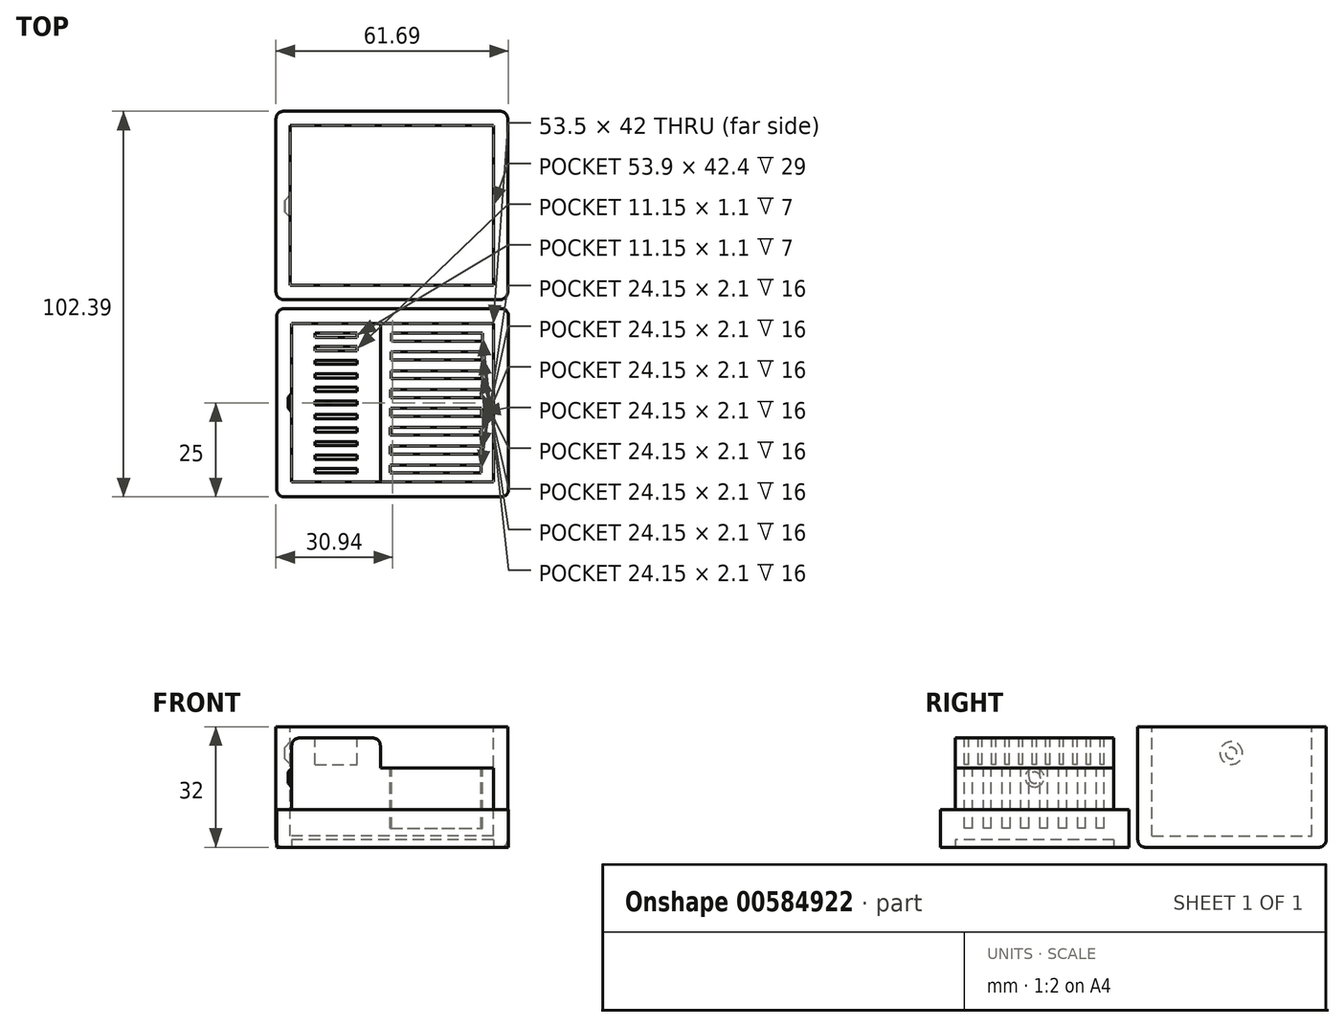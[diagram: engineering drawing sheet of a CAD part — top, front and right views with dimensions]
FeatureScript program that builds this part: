
annotation { "Feature Type Name" : "Feature", "Feature Type Description" : "" }
export const myFeature = defineFeature(function(context is Context, id is Id, definition is map)
    precondition{}
    {
        {
            var Q0;
            Q0=qCreatedBy(makeId("Top.planeOp"),FACE);
            var sketch = newSketch(context, id + "F0", { "sketchPlane" : qUnion([Q0])});
            skLineSegment(sketch, "E0.bottom", {"start": v(30.75, -25) * mm, "end": v(-30.75, -25) * mm});
            skLineSegment(sketch, "E0.top", {"start": v(30.75, 25) * mm, "end": v(-30.75, 25) * mm});
            skLineSegment(sketch, "E0.left", {"start": v(30.75, -25) * mm, "end": v(30.75, 25) * mm});
            skLineSegment(sketch, "E0.right", {"start": v(-30.75, -25) * mm, "end": v(-30.75, 25) * mm});
            skPoint(sketch, "E0.middle", {"position": v(0, 0) * mm});
            skSolve(sketch);
        }
        {
            var Q0;
            Q0 = qSketchRegion(id + "F0", true);
            extrude(context, id + "F1", {"entities" : qUnion([Q0]), "depth" : 21 * mm, "offsetDistance" : 25 * mm});
        }
        {
            var Q0;
            Q0=makeQuery(id+"F1.opExtrude","CAP_FACE",FACE,{"disambiguationData":[OSD([sQuery(id+"F0.wireOp",EDGE,"E0.bottom"),sQuery(id+"F0.wireOp",EDGE,"E0.top"),sQuery(id+"F0.wireOp",EDGE,"E0.left"),sQuery(id+"F0.wireOp",EDGE,"E0.right")])],"isStart":false});
            var sketch = newSketch(context, id + "F2", { "sketchPlane" : qUnion([Q0])});
            skLineSegment(sketch, "E1.bottom", {"start": v(26.75, -21) * mm, "end": v(-26.75, -21) * mm});
            skLineSegment(sketch, "E1.top", {"start": v(26.75, 21) * mm, "end": v(-26.75, 21) * mm});
            skLineSegment(sketch, "E1.left", {"start": v(26.75, -21) * mm, "end": v(26.75, 21) * mm});
            skLineSegment(sketch, "E1.right", {"start": v(-26.75, -21) * mm, "end": v(-26.75, 21) * mm});
            skPoint(sketch, "E1.middle", {"position": v(0, 0) * mm});
            skSolve(sketch);
        }
        {
            var Q0;
            Q0=makeQuery(id+"F2.imprint","IMPRINT",FACE,{"disambiguationData":[TD([[makeQuery(id+"F2.imprint","IMPRINT",EDGE,{"derivedFrom":sQuery(id+"F2.wireOp",EDGE,"E1.bottom")}),1.0]])]});
            extrude(context, id + "F3", {"entities" : qUnion([Q0]), "operationType" : NewBodyOperationType.REMOVE, "oppositeDirection" : true, "depth" : 11 * mm, "offsetDistance" : 25 * mm});
        }
        {
            var Q0;
            Q0=makeQuery(id+"F1.opExtrude","CAP_FACE",FACE,{"disambiguationData":[OSD([sQuery(id+"F0.wireOp",EDGE,"E0.bottom"),sQuery(id+"F0.wireOp",EDGE,"E0.top"),sQuery(id+"F0.wireOp",EDGE,"E0.left"),sQuery(id+"F0.wireOp",EDGE,"E0.right")])],"isStart":false});
            var sketch = newSketch(context, id + "F4", { "sketchPlane" : qUnion([Q0])});
            skLineSegment(sketch, "E2.bottom", {"start": v(0, 21) * mm, "end": v(-26.75, 21) * mm});
            skLineSegment(sketch, "E2.top", {"start": v(0, -21) * mm, "end": v(-26.75, -21) * mm});
            skLineSegment(sketch, "E2.right", {"start": v(-26.75, 21) * mm, "end": v(-26.75, -21) * mm});
            skLineSegment(sketch, "E3.bottom", {"start": v(-26.75, 21) * mm, "end": v(-3.25, 21) * mm});
            skLineSegment(sketch, "E3.top", {"start": v(-26.75, -21) * mm, "end": v(-3.25, -21) * mm});
            skLineSegment(sketch, "E3.right", {"start": v(-3.25, 21) * mm, "end": v(-3.25, -21) * mm});
            skSolve(sketch);
        }
        {
            var Q0;
            Q0 = qSketchRegion(id + "F4", true);
            extrude(context, id + "F5", {"entities" : qUnion([Q0]), "operationType" : NewBodyOperationType.ADD, "depth" : 8 * mm, "offsetDistance" : 25 * mm});
        }
        {
            var Q0;
            Q0=makeQuery(id+"F5.opExtrude","CAP_FACE",FACE,{"disambiguationData":[OSD([sQuery(id+"F4.wireOp",EDGE,"E3.bottom"),sQuery(id+"F4.wireOp",EDGE,"E3.top"),sQuery(id+"F4.wireOp",EDGE,"E2.right"),sQuery(id+"F4.wireOp",EDGE,"E3.right")])],"isStart":false});
            var sketch = newSketch(context, id + "F6", { "sketchPlane" : qUnion([Q0]), "disableImprinting" : false});
            skLineSegment(sketch, "E4.bottom", {"start": v(-20.57, 18.5) * mm, "end": v(-9.42, 18.5) * mm});
            skLineSegment(sketch, "E4.top", {"start": v(-20.57, 17.4) * mm, "end": v(-9.42, 17.4) * mm});
            skLineSegment(sketch, "E4.left", {"start": v(-20.57, 18.5) * mm, "end": v(-20.57, 17.4) * mm});
            skLineSegment(sketch, "E4.right", {"start": v(-9.42, 18.5) * mm, "end": v(-9.42, 17.4) * mm});
            skLineSegment(sketch, "E5.1.0.0", {"start": v(-20.57, 14.9) * mm, "end": v(-9.42, 14.9) * mm});
            skLineSegment(sketch, "E5.1.0.1", {"start": v(-20.57, 13.8) * mm, "end": v(-9.42, 13.8) * mm});
            skLineSegment(sketch, "E5.1.0.2", {"start": v(-9.42, 14.9) * mm, "end": v(-9.42, 13.8) * mm});
            skLineSegment(sketch, "E5.1.0.3", {"start": v(-20.57, 14.9) * mm, "end": v(-20.57, 13.8) * mm});
            skLineSegment(sketch, "E5.2.0.0", {"start": v(-20.57, 11.3) * mm, "end": v(-9.42, 11.3) * mm});
            skLineSegment(sketch, "E5.2.0.1", {"start": v(-20.57, 10.2) * mm, "end": v(-9.42, 10.2) * mm});
            skLineSegment(sketch, "E5.2.0.2", {"start": v(-9.42, 11.3) * mm, "end": v(-9.42, 10.2) * mm});
            skLineSegment(sketch, "E5.2.0.3", {"start": v(-20.57, 11.3) * mm, "end": v(-20.57, 10.2) * mm});
            skLineSegment(sketch, "E5.3.0.0", {"start": v(-20.57, 7.7) * mm, "end": v(-9.42, 7.7) * mm});
            skLineSegment(sketch, "E5.3.0.1", {"start": v(-20.57, 6.6) * mm, "end": v(-9.42, 6.6) * mm});
            skLineSegment(sketch, "E5.3.0.2", {"start": v(-9.42, 7.7) * mm, "end": v(-9.42, 6.6) * mm});
            skLineSegment(sketch, "E5.3.0.3", {"start": v(-20.57, 7.7) * mm, "end": v(-20.57, 6.6) * mm});
            skLineSegment(sketch, "E5.4.0.0", {"start": v(-20.57, 4.1) * mm, "end": v(-9.42, 4.1) * mm});
            skLineSegment(sketch, "E5.4.0.1", {"start": v(-20.57, 3) * mm, "end": v(-9.42, 3) * mm});
            skLineSegment(sketch, "E5.4.0.2", {"start": v(-9.42, 4.1) * mm, "end": v(-9.42, 3) * mm});
            skLineSegment(sketch, "E5.4.0.3", {"start": v(-20.57, 4.1) * mm, "end": v(-20.57, 3) * mm});
            skLineSegment(sketch, "E5.5.0.0", {"start": v(-20.57, 0.5) * mm, "end": v(-9.42, 0.5) * mm});
            skLineSegment(sketch, "E5.5.0.1", {"start": v(-20.57, -0.6) * mm, "end": v(-9.42, -0.6) * mm});
            skLineSegment(sketch, "E5.5.0.2", {"start": v(-9.42, 0.5) * mm, "end": v(-9.42, -0.6) * mm});
            skLineSegment(sketch, "E5.5.0.3", {"start": v(-20.57, 0.5) * mm, "end": v(-20.57, -0.6) * mm});
            skLineSegment(sketch, "E5.6.0.0", {"start": v(-20.57, -3.1) * mm, "end": v(-9.42, -3.1) * mm});
            skLineSegment(sketch, "E5.6.0.1", {"start": v(-20.57, -4.2) * mm, "end": v(-9.42, -4.2) * mm});
            skLineSegment(sketch, "E5.6.0.2", {"start": v(-9.42, -3.1) * mm, "end": v(-9.42, -4.2) * mm});
            skLineSegment(sketch, "E5.6.0.3", {"start": v(-20.57, -3.1) * mm, "end": v(-20.57, -4.2) * mm});
            skLineSegment(sketch, "E5.7.0.0", {"start": v(-20.57, -6.7) * mm, "end": v(-9.42, -6.7) * mm});
            skLineSegment(sketch, "E5.7.0.1", {"start": v(-20.57, -7.8) * mm, "end": v(-9.42, -7.8) * mm});
            skLineSegment(sketch, "E5.7.0.2", {"start": v(-9.42, -6.7) * mm, "end": v(-9.42, -7.8) * mm});
            skLineSegment(sketch, "E5.7.0.3", {"start": v(-20.57, -6.7) * mm, "end": v(-20.57, -7.8) * mm});
            skLineSegment(sketch, "E5.8.0.0", {"start": v(-20.57, -10.3) * mm, "end": v(-9.42, -10.3) * mm});
            skLineSegment(sketch, "E5.8.0.1", {"start": v(-20.57, -11.4) * mm, "end": v(-9.42, -11.4) * mm});
            skLineSegment(sketch, "E5.8.0.2", {"start": v(-9.42, -10.3) * mm, "end": v(-9.42, -11.4) * mm});
            skLineSegment(sketch, "E5.8.0.3", {"start": v(-20.57, -10.3) * mm, "end": v(-20.57, -11.4) * mm});
            skLineSegment(sketch, "E5.9.0.0", {"start": v(-20.57, -13.9) * mm, "end": v(-9.42, -13.9) * mm});
            skLineSegment(sketch, "E5.9.0.1", {"start": v(-20.57, -15) * mm, "end": v(-9.42, -15) * mm});
            skLineSegment(sketch, "E5.9.0.2", {"start": v(-9.42, -13.9) * mm, "end": v(-9.42, -15) * mm});
            skLineSegment(sketch, "E5.9.0.3", {"start": v(-20.57, -13.9) * mm, "end": v(-20.57, -15) * mm});
            skLineSegment(sketch, "E5.10.0.0", {"start": v(-20.57, -17.5) * mm, "end": v(-9.42, -17.5) * mm});
            skLineSegment(sketch, "E5.10.0.1", {"start": v(-20.57, -18.6) * mm, "end": v(-9.42, -18.6) * mm});
            skLineSegment(sketch, "E5.10.0.2", {"start": v(-9.42, -17.5) * mm, "end": v(-9.42, -18.6) * mm});
            skLineSegment(sketch, "E5.10.0.3", {"start": v(-20.57, -17.5) * mm, "end": v(-20.57, -18.6) * mm});
            skLineSegment(sketch, "E5.direction1", {"start": v(-17.32, 17.5) * mm, "end": v(-17.32, 13.9) * mm, "construction": true});
            skSolve(sketch);
        }
        {
            var Q0;
            Q0 = qSketchRegion(id + "F6", true);
            extrude(context, id + "F7", {"entities" : qUnion([Q0]), "operationType" : NewBodyOperationType.REMOVE, "oppositeDirection" : true, "depth" : 7 * mm, "offsetDistance" : 25 * mm});
        }
        {
            var Q0;
            Q0=makeQuery(id+"F1.opExtrude","CAP_FACE",FACE,{"disambiguationData":[OSD([sQuery(id+"F0.wireOp",EDGE,"E0.bottom"),sQuery(id+"F0.wireOp",EDGE,"E0.top"),sQuery(id+"F0.wireOp",EDGE,"E0.left"),sQuery(id+"F0.wireOp",EDGE,"E0.right")])],"isStart":false});
            var sketch = newSketch(context, id + "F8", { "sketchPlane" : qUnion([Q0])});
            skLineSegment(sketch, "E6.bottom", {"start": v(-0.33, 18.5) * mm, "end": v(23.82, 18.5) * mm});
            skLineSegment(sketch, "E6.top", {"start": v(-0.33, 16.4) * mm, "end": v(23.82, 16.4) * mm});
            skLineSegment(sketch, "E6.left", {"start": v(-0.33, 18.5) * mm, "end": v(-0.33, 16.4) * mm});
            skLineSegment(sketch, "E6.right", {"start": v(23.82, 18.5) * mm, "end": v(23.82, 16.4) * mm});
            skLineSegment(sketch, "E7.1.0.0", {"start": v(-0.38, 11.4) * mm, "end": v(23.77, 11.4) * mm});
            skLineSegment(sketch, "E7.1.0.1", {"start": v(23.77, 13.5) * mm, "end": v(23.77, 11.4) * mm});
            skLineSegment(sketch, "E7.1.0.2", {"start": v(-0.38, 13.5) * mm, "end": v(-0.38, 11.4) * mm});
            skLineSegment(sketch, "E7.1.0.3", {"start": v(-0.38, 13.5) * mm, "end": v(23.77, 13.5) * mm});
            skLineSegment(sketch, "E7.2.0.0", {"start": v(-0.44, 6.4) * mm, "end": v(23.71, 6.4) * mm});
            skLineSegment(sketch, "E7.2.0.1", {"start": v(23.71, 8.5) * mm, "end": v(23.71, 6.4) * mm});
            skLineSegment(sketch, "E7.2.0.2", {"start": v(-0.44, 8.5) * mm, "end": v(-0.44, 6.4) * mm});
            skLineSegment(sketch, "E7.2.0.3", {"start": v(-0.44, 8.5) * mm, "end": v(23.71, 8.5) * mm});
            skLineSegment(sketch, "E7.direction1", {"start": v(-0.33, 16.4) * mm, "end": v(-0.38, 11.4) * mm, "construction": true});
            skLineSegment(sketch, "E8.0.3.0", {"start": v(-0.5, 1.4) * mm, "end": v(23.66, 1.4) * mm});
            skLineSegment(sketch, "E8.3.3.0", {"start": v(23.66, 3.5) * mm, "end": v(23.66, 1.4) * mm});
            skLineSegment(sketch, "E8.6.3.0", {"start": v(-0.5, 3.5) * mm, "end": v(-0.5, 1.4) * mm});
            skLineSegment(sketch, "E8.9.3.0", {"start": v(-0.5, 3.5) * mm, "end": v(23.66, 3.5) * mm});
            skLineSegment(sketch, "E8.0.4.0", {"start": v(-0.55, -3.6) * mm, "end": v(23.6, -3.6) * mm});
            skLineSegment(sketch, "E8.3.4.0", {"start": v(23.6, -1.5) * mm, "end": v(23.6, -3.6) * mm});
            skLineSegment(sketch, "E8.6.4.0", {"start": v(-0.55, -1.5) * mm, "end": v(-0.55, -3.6) * mm});
            skLineSegment(sketch, "E8.9.4.0", {"start": v(-0.55, -1.5) * mm, "end": v(23.6, -1.5) * mm});
            skLineSegment(sketch, "E8.0.5.0", {"start": v(-0.6, -8.6) * mm, "end": v(23.55, -8.6) * mm});
            skLineSegment(sketch, "E8.3.5.0", {"start": v(23.55, -6.5) * mm, "end": v(23.55, -8.6) * mm});
            skLineSegment(sketch, "E8.6.5.0", {"start": v(-0.6, -6.5) * mm, "end": v(-0.6, -8.6) * mm});
            skLineSegment(sketch, "E8.9.5.0", {"start": v(-0.6, -6.5) * mm, "end": v(23.55, -6.5) * mm});
            skLineSegment(sketch, "E9.0.6.0", {"start": v(-0.66, -13.6) * mm, "end": v(23.5, -13.6) * mm});
            skLineSegment(sketch, "E9.3.6.0", {"start": v(23.5, -11.5) * mm, "end": v(23.5, -13.6) * mm});
            skLineSegment(sketch, "E9.6.6.0", {"start": v(-0.66, -11.5) * mm, "end": v(-0.66, -13.6) * mm});
            skLineSegment(sketch, "E9.9.6.0", {"start": v(-0.66, -11.5) * mm, "end": v(23.5, -11.5) * mm});
            skLineSegment(sketch, "E10.0.7.0", {"start": v(-0.71, -18.6) * mm, "end": v(23.44, -18.6) * mm});
            skLineSegment(sketch, "E10.3.7.0", {"start": v(23.44, -16.5) * mm, "end": v(23.44, -18.6) * mm});
            skLineSegment(sketch, "E10.6.7.0", {"start": v(-0.71, -16.5) * mm, "end": v(-0.71, -18.6) * mm});
            skLineSegment(sketch, "E10.9.7.0", {"start": v(-0.71, -16.5) * mm, "end": v(23.44, -16.5) * mm});
            skSolve(sketch);
        }
        {
            var Q0;
            Q0 = qSketchRegion(id + "F8", true);
            extrude(context, id + "F9", {"entities" : qUnion([Q0]), "operationType" : NewBodyOperationType.REMOVE, "oppositeDirection" : true, "depth" : 16 * mm, "offsetDistance" : 25 * mm});
        }
        {
            var Q0;
            Q0=makeQuery(id+"F5.opExtrude","CAP_EDGE",EDGE,{"disambiguationData":[OSD([sQuery(id+"F4.wireOp",EDGE,"E3.right")])],"isStart":false});
            var Q1;
            Q1=makeQuery(id+"F3.boolean.opBoolean","COPY",EDGE,{"derivedFrom":makeQuery(id+"F3.opExtrude","CAP_EDGE",EDGE,{"disambiguationData":[OSD([sQuery(id+"F2.wireOp",EDGE,"E1.left")])],"isStart":true})});
            var Q2;
            Q2=makeQuery(id+"F5.opExtrude","CAP_EDGE",EDGE,{"disambiguationData":[OSD([sQuery(id+"F4.wireOp",EDGE,"E2.right")])],"isStart":false});
            var Q3;
            Q3=makeQuery(id+"F5.opExtrude","CAP_EDGE",EDGE,{"disambiguationData":[OSD([sQuery(id+"F4.wireOp",EDGE,"E3.right")])],"isStart":true});
            var Q4;
            Q4=makeQuery(id+"F1.opExtrude","SWEPT_EDGE",EDGE,{"disambiguationData":[OSD([sQuery(id+"F0.wireOp",EDGE,"E0.bottom"),sQuery(id+"F0.wireOp",EDGE,"E0.right")])]});
            var Q5;
            Q5=makeQuery(id+"F1.opExtrude","SWEPT_EDGE",EDGE,{"disambiguationData":[OSD([sQuery(id+"F0.wireOp",EDGE,"E0.top"),sQuery(id+"F0.wireOp",EDGE,"E0.right")])]});
            var Q6;
            Q6=makeQuery(id+"F1.opExtrude","SWEPT_EDGE",EDGE,{"disambiguationData":[OSD([sQuery(id+"F0.wireOp",EDGE,"E0.bottom"),sQuery(id+"F0.wireOp",EDGE,"E0.left")])]});
            var Q7;
            Q7=makeQuery(id+"F1.opExtrude","SWEPT_EDGE",EDGE,{"disambiguationData":[OSD([sQuery(id+"F0.wireOp",EDGE,"E0.top"),sQuery(id+"F0.wireOp",EDGE,"E0.left")])]});
            var Q8;
            Q8=makeQuery(id+"F5.opExtrude","CAP_EDGE",EDGE,{"disambiguationData":[OSD([sQuery(id+"F4.wireOp",EDGE,"E3.top")])],"isStart":false});
            var Q9;
            Q9=makeQuery(id+"F3.boolean.opBoolean","COPY",EDGE,{"derivedFrom":makeQuery(id+"F3.opExtrude","CAP_EDGE",EDGE,{"disambiguationData":[OSD([sQuery(id+"F2.wireOp",EDGE,"E1.bottom")])],"isStart":true})});
            var Q10;
            Q10=makeQuery(id+"F3.boolean.opBoolean","COPY",EDGE,{"derivedFrom":makeQuery(id+"F3.opExtrude","CAP_EDGE",EDGE,{"disambiguationData":[OSD([sQuery(id+"F2.wireOp",EDGE,"E1.top")])],"isStart":true})});
            var Q11;
            Q11=makeQuery(id+"F5.opExtrude","CAP_EDGE",EDGE,{"disambiguationData":[OSD([sQuery(id+"F4.wireOp",EDGE,"E3.bottom")])],"isStart":false});
            fillet(context, id + "F10", {"entities" : qUnion([Q0, Q1, Q2, Q3, Q4, Q5, Q6, Q7, Q8, Q9, Q10, Q11]), "radius" : 2 * mm, "tangentPropagation" : true, "allowEdgeOverflow" : false});
        }
        {
            var Q0;
            Q0=qCreatedBy(makeId("Top.planeOp"),FACE);
            var sketch = newSketch(context, id + "F11", { "sketchPlane" : qUnion([Q0])});
            skLineSegment(sketch, "E11.bottom", {"start": v(-30.94, 77.39) * mm, "end": v(30.56, 77.39) * mm});
            skLineSegment(sketch, "E11.top", {"start": v(-30.94, 27.39) * mm, "end": v(30.56, 27.39) * mm});
            skLineSegment(sketch, "E11.left", {"start": v(-30.94, 77.39) * mm, "end": v(-30.94, 27.39) * mm});
            skLineSegment(sketch, "E11.right", {"start": v(30.56, 77.39) * mm, "end": v(30.56, 27.39) * mm});
            skSolve(sketch);
        }
        {
            var Q0;
            Q0 = qSketchRegion(id + "F11", true);
            extrude(context, id + "F12", {"entities" : qUnion([Q0]), "depth" : 32 * mm, "offsetDistance" : 25 * mm});
        }
        {
            var Q0;
            Q0=makeQuery(id+"F12.opExtrude","CAP_FACE",FACE,{"disambiguationData":[OSD([sQuery(id+"F11.wireOp",EDGE,"E11.bottom"),sQuery(id+"F11.wireOp",EDGE,"E11.top"),sQuery(id+"F11.wireOp",EDGE,"E11.left"),sQuery(id+"F11.wireOp",EDGE,"E11.right")])],"isStart":false});
            var sketch = newSketch(context, id + "F13", { "sketchPlane" : qUnion([Q0])});
            skLineSegment(sketch, "E12.bottom", {"start": v(26.76, 31.19) * mm, "end": v(-27.14, 31.19) * mm});
            skLineSegment(sketch, "E12.top", {"start": v(26.76, 73.59) * mm, "end": v(-27.14, 73.59) * mm});
            skLineSegment(sketch, "E12.left", {"start": v(26.76, 31.19) * mm, "end": v(26.76, 73.59) * mm});
            skLineSegment(sketch, "E12.right", {"start": v(-27.14, 31.19) * mm, "end": v(-27.14, 73.59) * mm});
            skPoint(sketch, "E12.middle", {"position": v(-0.2, 52.39) * mm});
            skPoint(sketch, "E12.middle.positionSnap0", {"position": v(-30.94, 52.39) * mm});
            skPoint(sketch, "E12.middle.positionSnap1", {"position": v(-0.2, 77.39) * mm});
            skPoint(sketch, "E12.centerSnap0", {"position": v(-30.94, 52.39) * mm});
            skPoint(sketch, "E12.centerSnap1", {"position": v(-0.2, 77.39) * mm});
            skSolve(sketch);
        }
        {
            var Q0;
            Q0 = qSketchRegion(id + "F13", true);
            extrude(context, id + "F14", {"entities" : qUnion([Q0]), "operationType" : NewBodyOperationType.REMOVE, "oppositeDirection" : true, "depth" : 29 * mm, "offsetDistance" : 25 * mm});
        }
        {
            var Q0;
            Q0=makeQuery(id+"F5.boolean.opBoolean","MERGE",FACE,{"derivedFrom":[makeQuery(id+"F3.boolean.opBoolean","COPY",FACE,{"derivedFrom":makeQuery(id+"F3.opExtrude","SWEPT_FACE",FACE,{"disambiguationData":[OSD([sQuery(id+"F2.wireOp",EDGE,"E1.right")])]})}),makeQuery(id+"F5.opExtrude","SWEPT_FACE",FACE,{"disambiguationData":[OSD([sQuery(id+"F4.wireOp",EDGE,"E2.right")])]})]});
            var sketch = newSketch(context, id + "F15", { "sketchPlane" : qUnion([Q0])});
            skCircle(sketch, "E13", {"center": v(0, 18.5) * mm, "radius": 2.5 * mm});
            skPoint(sketch, "E13.centerSnap0", {"position": v(-21, 18.5) * mm});
            skPoint(sketch, "E13.centerSnap1", {"position": v(0, 27) * mm});
            skSolve(sketch);
        }
        {
            var Q0;
            Q0 = qSketchRegion(id + "F15", true);
            extrude(context, id + "F16", {"entities" : qUnion([Q0]), "operationType" : NewBodyOperationType.ADD, "depth" : 1 * mm, "offsetDistance" : 25 * mm, "hasDraft" : true, "draftAngle" : 45 * degree, "draftPullDirection" : true});
        }
        {
            var Q0;
            Q0=makeQuery(id+"F14.boolean.opBoolean","COPY",FACE,{"derivedFrom":makeQuery(id+"F14.opExtrude","SWEPT_FACE",FACE,{"disambiguationData":[OSD([sQuery(id+"F13.wireOp",EDGE,"E12.right")])]})});
            var sketch = newSketch(context, id + "F17", { "sketchPlane" : qUnion([Q0])});
            skCircle(sketch, "E14", {"center": v(52.19, 25) * mm, "radius": 3 * mm});
            skSolve(sketch);
        }
        {
            var Q0;
            Q0 = qSketchRegion(id + "F17", true);
            extrude(context, id + "F18", {"entities" : qUnion([Q0]), "operationType" : NewBodyOperationType.REMOVE, "oppositeDirection" : true, "depth" : 1.5 * mm, "offsetDistance" : 25 * mm, "hasDraft" : true, "draftAngle" : 45 * degree, "draftPullDirection" : true});
        }
        {
            var Q0;
            Q0=makeQuery(id+"F12.opExtrude","CAP_FACE",FACE,{"disambiguationData":[OSD([sQuery(id+"F11.wireOp",EDGE,"E11.bottom"),sQuery(id+"F11.wireOp",EDGE,"E11.top"),sQuery(id+"F11.wireOp",EDGE,"E11.left"),sQuery(id+"F11.wireOp",EDGE,"E11.right")])],"isStart":true});
            var Q1;
            Q1=makeQuery(id+"F12.opExtrude","SWEPT_EDGE",EDGE,{"disambiguationData":[OSD([sQuery(id+"F11.wireOp",EDGE,"E11.bottom"),sQuery(id+"F11.wireOp",EDGE,"E11.left")])]});
            var Q2;
            Q2=makeQuery(id+"F12.opExtrude","SWEPT_EDGE",EDGE,{"disambiguationData":[OSD([sQuery(id+"F11.wireOp",EDGE,"E11.top"),sQuery(id+"F11.wireOp",EDGE,"E11.left")])]});
            var Q3;
            Q3=makeQuery(id+"F12.opExtrude","SWEPT_EDGE",EDGE,{"disambiguationData":[OSD([sQuery(id+"F11.wireOp",EDGE,"E11.top"),sQuery(id+"F11.wireOp",EDGE,"E11.right")])]});
            var Q4;
            Q4=makeQuery(id+"F12.opExtrude","SWEPT_EDGE",EDGE,{"disambiguationData":[OSD([sQuery(id+"F11.wireOp",EDGE,"E11.bottom"),sQuery(id+"F11.wireOp",EDGE,"E11.right")])]});
            fillet(context, id + "F19", {"entities" : qUnion([Q0, Q1, Q2, Q3, Q4]), "radius" : 2 * mm, "tangentPropagation" : true, "allowEdgeOverflow" : false});
        }
        {
            var Q0;
            Q0=makeQuery(id+"F1.opExtrude","CAP_FACE",FACE,{"disambiguationData":[OSD([sQuery(id+"F0.wireOp",EDGE,"E0.bottom"),sQuery(id+"F0.wireOp",EDGE,"E0.top"),sQuery(id+"F0.wireOp",EDGE,"E0.left"),sQuery(id+"F0.wireOp",EDGE,"E0.right")])],"isStart":true});
            var sketch = newSketch(context, id + "F20", { "sketchPlane" : qUnion([Q0])});
            skLineSegment(sketch, "E15.bottom", {"start": v(26.75, -21) * mm, "end": v(-26.75, -21) * mm});
            skLineSegment(sketch, "E15.top", {"start": v(26.75, 21) * mm, "end": v(-26.75, 21) * mm});
            skLineSegment(sketch, "E15.left", {"start": v(26.75, -21) * mm, "end": v(26.75, 21) * mm});
            skLineSegment(sketch, "E15.right", {"start": v(-26.75, -21) * mm, "end": v(-26.75, 21) * mm});
            skPoint(sketch, "E15.middle", {"position": v(0, 0) * mm});
            skSolve(sketch);
        }
        {
            var Q0;
            Q0=makeQuery(id+"F20.imprint","IMPRINT",FACE,{"disambiguationData":[TD([[makeQuery(id+"F20.imprint","IMPRINT",EDGE,{"derivedFrom":sQuery(id+"F20.wireOp",EDGE,"E15.bottom")}),-1.0]])]});
            extrude(context, id + "F21", {"entities" : qUnion([Q0]), "operationType" : NewBodyOperationType.REMOVE, "oppositeDirection" : true, "depth" : 2 * mm, "offsetDistance" : 25 * mm});
        }
    });
